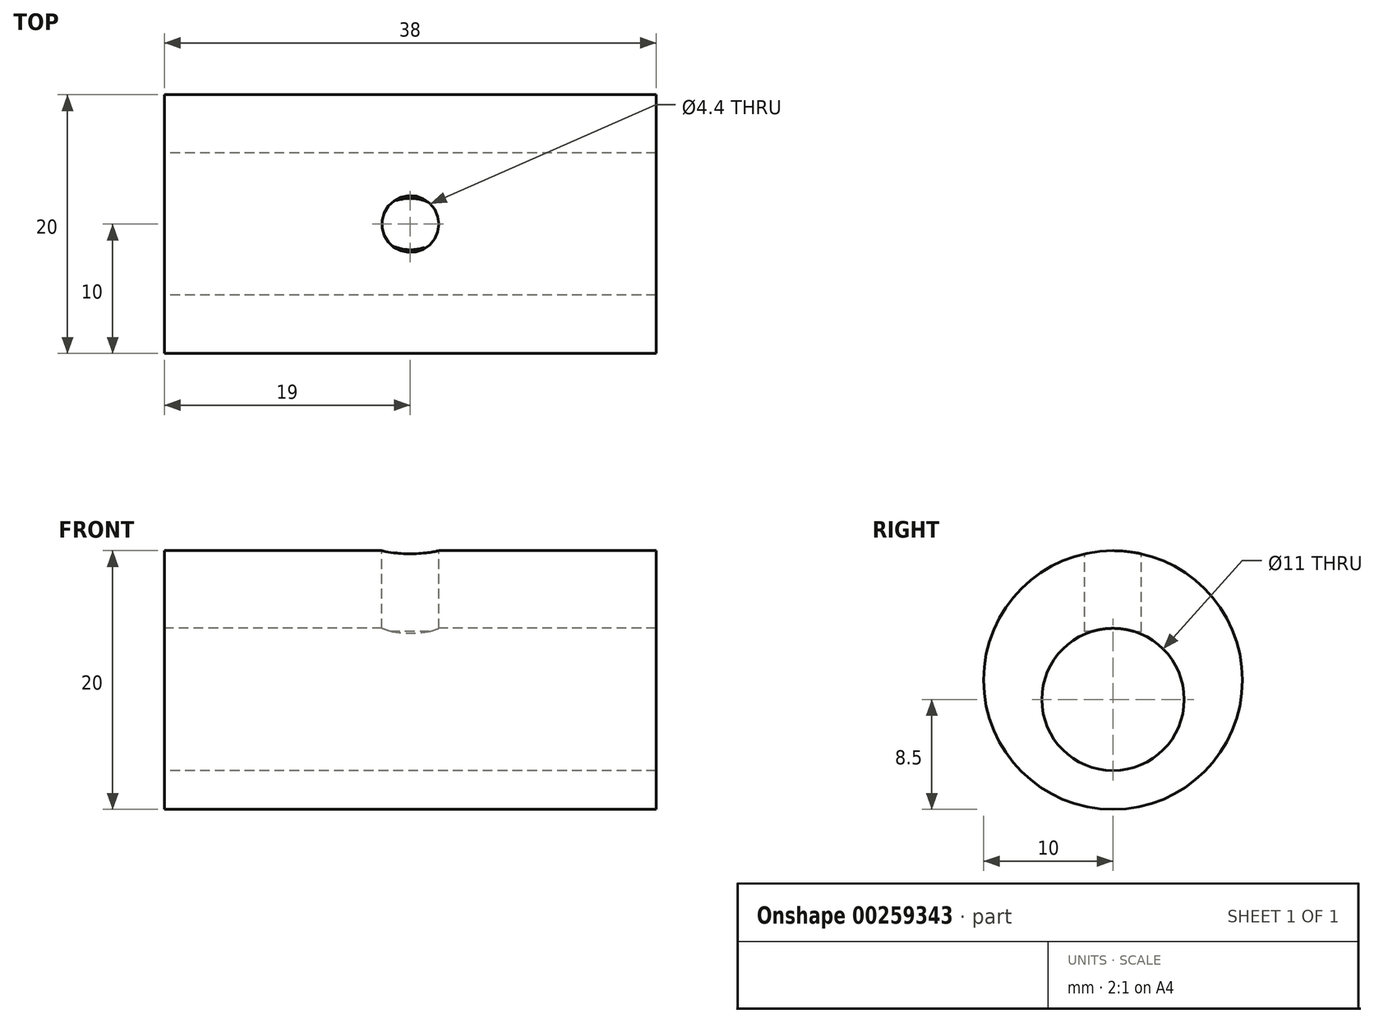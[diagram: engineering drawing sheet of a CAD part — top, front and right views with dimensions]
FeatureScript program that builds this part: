
annotation { "Feature Type Name" : "Feature", "Feature Type Description" : "" }
export const myFeature = defineFeature(function(context is Context, id is Id, definition is map)
    precondition{}
    {
        {
            var Q0;
            Q0=qCreatedBy(makeId("Right.planeOp"),FACE);
            var sketch = newSketch(context, id + "F0", { "sketchPlane" : qUnion([Q0])});
            skCircle(sketch, "E0", {"center": v(0, 0) * mm, "radius": 10 * mm});
            skCircle(sketch, "E1", {"center": v(0, -1.5) * mm, "radius": 5.5 * mm});
            skSolve(sketch);
        }
        {
            var Q0;
            Q0=makeQuery(id+"F0.imprint","IMPRINT",FACE,{"disambiguationData":[TD([[makeQuery(id+"F0.imprint","IMPRINT",EDGE,{"derivedFrom":sQuery(id+"F0.wireOp",EDGE,"E0")}),1.0]])]});
            extrude(context, id + "F1", {"entities" : qUnion([Q0]), "endBound" : BoundingType.SYMMETRIC, "depth" : 38 * mm});
        }
        {
            var Q0;
            Q0=qCreatedBy(makeId("Top.planeOp"),FACE);
            cPlane(context, id + "F2", {"entities" : qUnion([Q0]), "cplaneType" : CPlaneType.OFFSET, "offset" : 10 * mm, "width" : 150 * mm, "height" : 150 * mm});
        }
        {
            var Q0;
            Q0=qCreatedBy(id+"F2.planeOp",FACE);
            var sketch = newSketch(context, id + "F3", { "sketchPlane" : qUnion([Q0])});
            skCircle(sketch, "E2", {"center": v(0, 0) * mm, "radius": 5 * mm, "construction": true});
            skLineSegment(sketch, "E3", {"start": v(0, 0) * mm, "end": v(19.25, 0) * mm, "construction": true});
            skLineSegment(sketch, "E4", {"start": v(0, 0) * mm, "end": v(0, -9.9) * mm, "construction": true});
            skSolve(sketch);
        }
        {
            var Q0;
            Q0=sQuery(id+"F3.wireOp",VERTEX,"E2.center");
            var Q1;
            Q1=makeQuery(id+"F1.opExtrude","SWEPT_BODY",BODY,{"disambiguationData":[OSD([sQuery(id+"F0.wireOp",EDGE,"E0"),sQuery(id+"F0.wireOp",EDGE,"E1")])]});
            hole(context, id + "F4", {"style" : HoleStyle.SIMPLE, "endStyle" : HoleEndStyle.BLIND, "standardTappedOrClearance" : lookupTablePath({ "standard" : "ISO", "fit" : "Normal", "size" : "M4", "type" : "Clearance" }), "standardBlindInLast" : lookupTablePath({ "fit" : "Standard", "standard" : "ISO", "size" : "M4", "type" : "Clearance" }), "holeDiameter" : 4.4 * mm, "holeDepth" : 6 * mm, "tappedDepth" : 12 * mm, "tapClearance" : 3, "locations" : qUnion([Q0]), "scope" : qUnion([Q1])});
        }
    });
